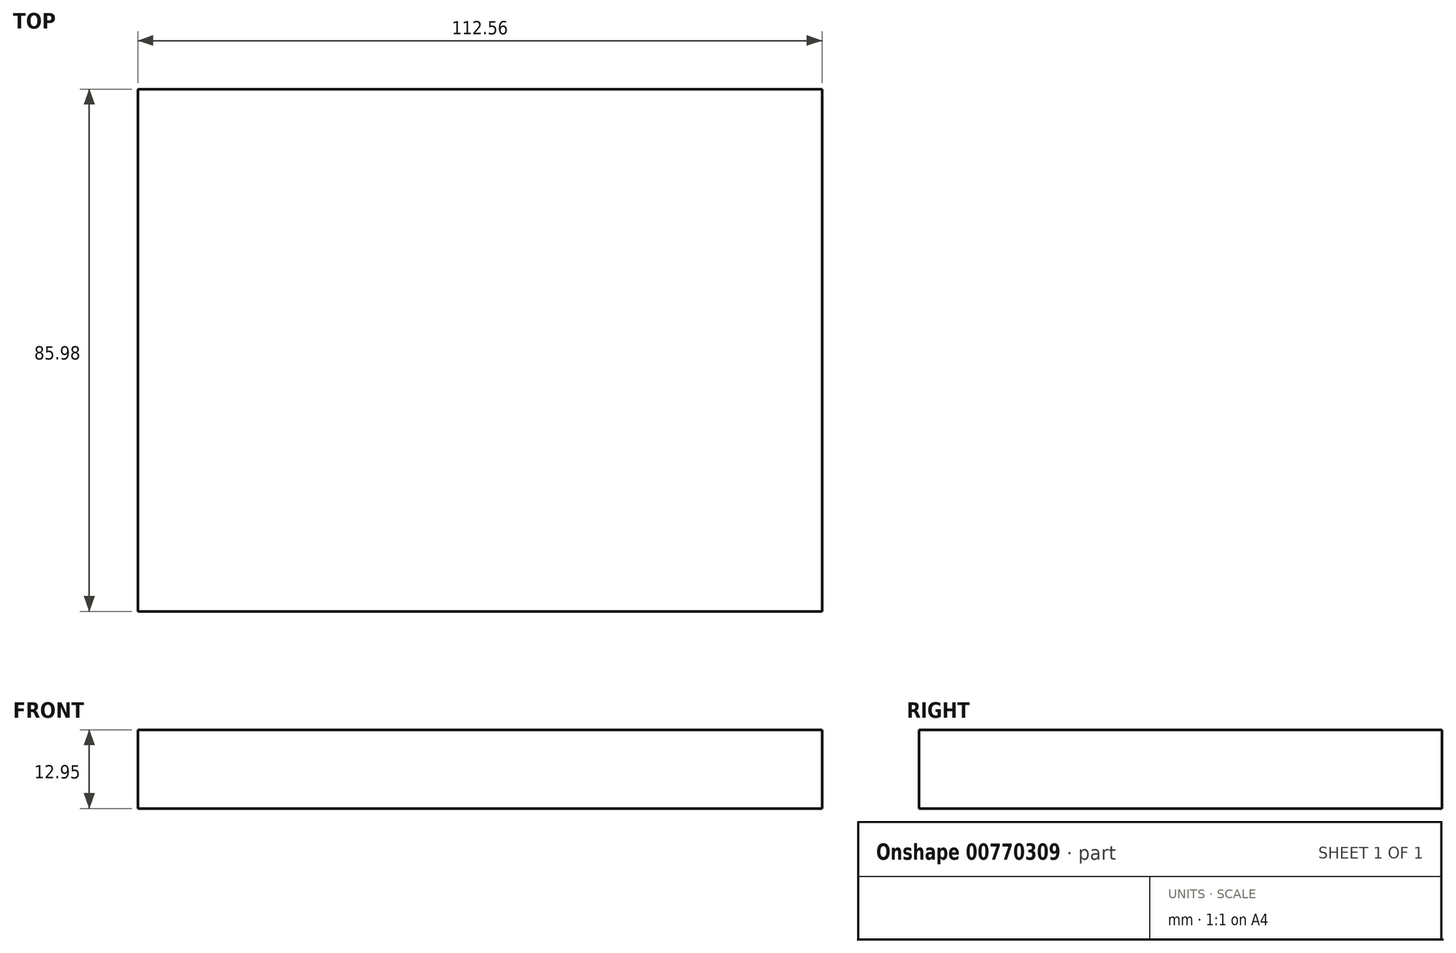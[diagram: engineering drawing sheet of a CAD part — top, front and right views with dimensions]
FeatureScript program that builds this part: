
annotation { "Feature Type Name" : "Feature", "Feature Type Description" : "" }
export const myFeature = defineFeature(function(context is Context, id is Id, definition is map)
    precondition{}
    {
        {
            var Q0;
            Q0=qCreatedBy(makeId("Top.planeOp"),FACE);
            var sketch = newSketch(context, id + "F0", { "sketchPlane" : qUnion([Q0])});
            skLineSegment(sketch, "E0.bottom", {"start": v(-56.28, -43) * mm, "end": v(56.28, -43) * mm});
            skLineSegment(sketch, "E0.top", {"start": v(-56.28, 43) * mm, "end": v(56.28, 43) * mm});
            skLineSegment(sketch, "E0.left", {"start": v(-56.28, -43) * mm, "end": v(-56.28, 43) * mm});
            skLineSegment(sketch, "E0.right", {"start": v(56.28, -43) * mm, "end": v(56.28, 43) * mm});
            skPoint(sketch, "E0.middle", {"position": v(0, 0) * mm});
            skSolve(sketch);
        }
        {
            var Q0;
            Q0 = qSketchRegion(id + "F0", true);
            extrude(context, id + "F1", {"entities" : qUnion([Q0]), "depth" : 25 * mm, "offsetDistance" : 25 * mm});
        }
        {
            var Q0;
            Q0=makeQuery(id+"F1.opExtrude","CAP_FACE",FACE,{"disambiguationData":[OSD([sQuery(id+"F0.wireOp",EDGE,"E0.bottom"),sQuery(id+"F0.wireOp",EDGE,"E0.top"),sQuery(id+"F0.wireOp",EDGE,"E0.left"),sQuery(id+"F0.wireOp",EDGE,"E0.right")])],"isStart":false});
            var sketch = newSketch(context, id + "F2", { "sketchPlane" : qUnion([Q0])});
            skCircle(sketch, "E1", {"center": v(37.75, -25.86) * mm, "radius": 5 * mm});
            skSolve(sketch);
        }
        {
            var Q0;
            Q0=makeQuery(id+"F2.imprint","IMPRINT",FACE,{"disambiguationData":[TD([[makeQuery(id+"F2.imprint","IMPRINT",EDGE,{"derivedFrom":sQuery(id+"F2.wireOp",EDGE,"E1")}),1.0]])]});
            var Q1;
            Q1=sQuery(id+"F2.wireOp",EDGE,"E1");
            extrude(context, id + "F3", {"entities" : qUnion([Q0]), "operationType" : NewBodyOperationType.REMOVE, "surfaceEntities" : qUnion([Q1]), "oppositeDirection" : true, "depth" : 10 * mm, "offsetDistance" : 25 * mm});
        }
        {
            var Q0;
            Q0=makeQuery(id+"F3.boolean.opBoolean","COPY",FACE,{"derivedFrom":makeQuery(id+"F3.opExtrude","CAP_FACE",FACE,{"disambiguationData":[OSD([sQuery(id+"F2.wireOp",EDGE,"E1")])],"isStart":false})});
            var sketch = newSketch(context, id + "F4", { "sketchPlane" : qUnion([Q0])});
            skCircle(sketch, "E2", {"center": v(37.75, -25.86) * mm, "radius": 4.08 * mm});
            skSolve(sketch);
        }
        {
            var Q0;
            Q0 = qSketchRegion(id + "F4", true);
            extrude(context, id + "F5", {"entities" : qUnion([Q0]), "operationType" : NewBodyOperationType.ADD, "depth" : 8.16 * mm, "offsetDistance" : 25 * mm});
        }
        {
            var Q0;
            Q0=makeQuery(id+"F2.imprint","IMPRINT",FACE,{"disambiguationData":[TD([[makeQuery(id+"F2.imprint","IMPRINT",EDGE,{"derivedFrom":sQuery(id+"F2.wireOp",EDGE,"E1")}),1.0]])]});
            var Q1;
            Q1=makeQuery(id+"F2.imprint","IMPRINT",FACE,{"disambiguationData":[TD([[makeQuery(id+"F2.imprint","IMPRINT",EDGE,{"derivedFrom":sQuery(id+"F2.wireOp",EDGE,"E1")}),-1.0]])]});
            var Q2;
            Q2=sQuery(id+"F2.wireOp",EDGE,"E1");
            extrude(context, id + "F6", {"entities" : qUnion([Q0, Q1]), "operationType" : NewBodyOperationType.REMOVE, "surfaceEntities" : qUnion([Q2]), "oppositeDirection" : true, "depth" : 12.05 * mm, "offsetDistance" : 25 * mm});
        }
    });
